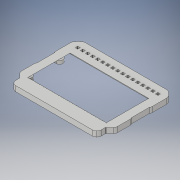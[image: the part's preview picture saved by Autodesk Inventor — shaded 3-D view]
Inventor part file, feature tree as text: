
AUTODESK INVENTOR PART (.ipt)
format: ipt  version: 2017 (Build 210142000, 142)  size: 624,640 bytes
history: native  units: mm
features: other x3, sketch x1
ambient origin geometry x8: Origin, YZ Plane, XZ Plane, XY Plane, X Axis, Y Axis, Z Axis, Center Point
bodies: Volumenkörper1 (feature_tree)
feature tree (4):
  other  "Gehäuse.iam"
  other  "Deckel.ipt:1"
  other  "DummyAuschnitt2.ipt:1"
  sketch  "Skizze 3"  dims[d0=10.0mm]
